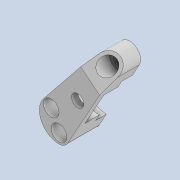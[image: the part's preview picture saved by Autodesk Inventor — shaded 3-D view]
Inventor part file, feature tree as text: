
AUTODESK INVENTOR PART (.ipt)
format: ipt  version: 2020.4 (Build 244396000, 396)  size: 192,000 bytes
history: native  units: mm
features: extrude x5, sketch x5
ambient origin geometry x8: Origin, YZ Plane, XZ Plane, XY Plane, X Axis, Y Axis, Z Axis, Center Point
bodies: Solid1 (feature_tree)
feature tree (10):
  extrude  "Extrusion1"  Depth=24.0mm
  extrude  "Extrusion2"  Depth=3.0mm
  extrude  "Extrusion3"  Depth=2.1mm
  extrude  "Extrusion4"  Depth=2.5mm
  extrude  "Extrusion5"  Depth=10.0mm
  sketch  "Sketch1"  dims[d0=18.0mm d1=24.0mm]
  sketch  "Sketch3"  dims[d2=2.1mm d3=3.0mm]
  sketch  "Sketch5"  dims[d4=3.0mm d5=2.1mm]
  sketch  "Sketch6"  dims[d6=2.1mm d7=2.5mm]
  sketch  "Sketch8"  dims[d8=5.0mm d9=3.0mm d10=7.0mm d12=10.0mm d15=6.0mm d16=8.0mm d17=0.0mm d18=3.1mm d25=5.5mm d26=10.0mm d27=14.9mm d28=2.7mm d29=0.0mm d30=12.0mm d31=8.251mm d32=4.0mm d33=4.0mm d34=4.0mm d35=4.9mm d36=0.0mm d37=11.4mm d38=3.65mm d39=0.0mm d40=10.0mm d41=0.0mm]
